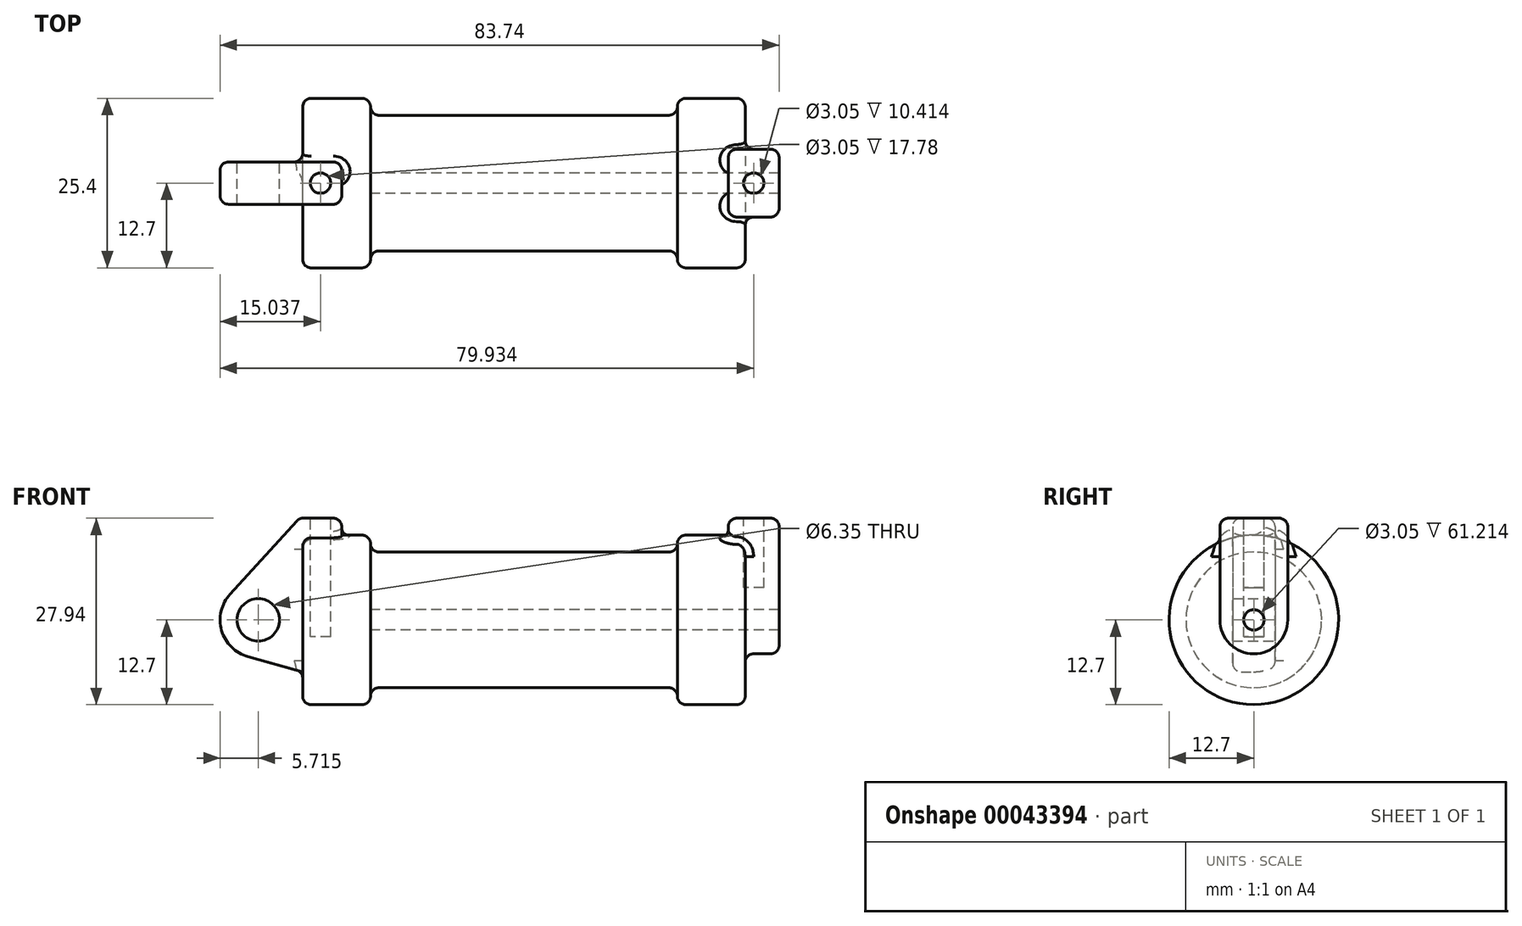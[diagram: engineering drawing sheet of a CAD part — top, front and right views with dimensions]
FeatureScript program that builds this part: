
annotation { "Feature Type Name" : "Feature", "Feature Type Description" : "" }
export const myFeature = defineFeature(function(context is Context, id is Id, definition is map)
    precondition{}
    {
        {
            var Q0;
            Q0=qCreatedBy(makeId("Front.planeOp"),FACE);
            var sketch = newSketch(context, id + "F0", { "sketchPlane" : qUnion([Q0])});
            skLineSegment(sketch, "E0", {"start": v(0, 0) * mm, "end": v(0, 12.7) * mm});
            skLineSegment(sketch, "E1", {"start": v(0, 12.7) * mm, "end": v(10.16, 12.7) * mm});
            skLineSegment(sketch, "E2", {"start": v(10.16, 12.7) * mm, "end": v(10.16, 10.16) * mm});
            skLineSegment(sketch, "E3", {"start": v(10.16, 10.16) * mm, "end": v(56.13, 10.16) * mm});
            skLineSegment(sketch, "E4", {"start": v(56.13, 10.16) * mm, "end": v(56.13, 12.7) * mm});
            skLineSegment(sketch, "E5", {"start": v(56.13, 12.7) * mm, "end": v(66.3, 12.7) * mm});
            skLineSegment(sketch, "E6", {"start": v(66.3, 12.7) * mm, "end": v(66.3, 0) * mm});
            skLineSegment(sketch, "E7", {"start": v(66.3, 0) * mm, "end": v(0, 0) * mm});
            skLineSegment(sketch, "E8", {"start": v(5.84, 15.24) * mm, "end": v(-0.5, 15.24) * mm});
            skLineSegment(sketch, "E9", {"start": v(-0.5, 15.24) * mm, "end": v(-10.88, 3.85) * mm});
            skLineSegment(sketch, "E10", {"start": v(0, 0) * mm, "end": v(-6.65, 0) * mm});
            skCircle(sketch, "E11", {"center": v(-6.65, 0) * mm, "radius": 5.72 * mm});
            skCircle(sketch, "E12", {"center": v(-6.65, 0) * mm, "radius": 3.18 * mm});
            skLineSegment(sketch, "E13", {"start": v(5.84, 15.24) * mm, "end": v(5.84, -9.4) * mm});
            skLineSegment(sketch, "E14", {"start": v(5.84, -9.4) * mm, "end": v(-8.18, -5.5) * mm});
            skSolve(sketch);
        }
        {
            var Q0;
            {var subQ6=sQuery(id+"F0.wireOp",EDGE,"E2");Q0=makeQuery(id+"F0.imprint","IMPRINT",FACE,{"disambiguationData":[TD([[makeQuery(id+"F0.imprint","IMPRINT",EDGE,{"derivedFrom":subQ6}),-1.0]])]});}
            var Q1;
            {var subQ5=sQuery(id+"F0.wireOp",EDGE,"E0");Q1=makeQuery(id+"F0.imprint","IMPRINT",FACE,{"disambiguationData":[TD([[makeQuery(id+"F0.imprint","IMPRINT",EDGE,{"derivedFrom":subQ5}),-1.0]])]});}
            var Q2;
            Q2=sQuery(id+"F0.wireOp",EDGE,"E7");
            revolve(context, id + "F1", {"entities" : qUnion([Q0, Q1]), "axis" : qUnion([Q2]), "revolveType" : RevolveType.FULL});
        }
        {
            var Q0;
            {var subQ8=sQuery(id+"F0.wireOp",EDGE,"E0");Q0=makeQuery(id+"F0.imprint","IMPRINT",FACE,{"disambiguationData":[TD([[makeQuery(id+"F0.imprint","IMPRINT",EDGE,{"derivedFrom":subQ8}),1.0]])]});}
            var Q1;
            {var subQ0=sQuery(id+"F0.wireOp",EDGE,"E12");Q1=makeQuery(id+"F0.imprint","IMPRINT",FACE,{"disambiguationData":[TD([[makeQuery(id+"F0.imprint","IMPRINT",EDGE,{"derivedFrom":subQ0}),-1.0]])]});}
            var Q2;
            {var subQ0=sQuery(id+"F0.wireOp",EDGE,"E14");Q2=makeQuery(id+"F0.imprint","IMPRINT",FACE,{"disambiguationData":[TD([[makeQuery(id+"F0.imprint","IMPRINT",EDGE,{"derivedFrom":subQ0}),-1.0]])]});}
            var Q3;
            {var subQ5=sQuery(id+"F0.wireOp",EDGE,"E0");Q3=makeQuery(id+"F0.imprint","IMPRINT",FACE,{"disambiguationData":[TD([[makeQuery(id+"F0.imprint","IMPRINT",EDGE,{"derivedFrom":subQ5}),-1.0]])]});}
            extrude(context, id + "F2", {"entities" : qUnion([Q0, Q1, Q2, Q3]), "operationType" : NewBodyOperationType.ADD, "endBound" : BoundingType.SYMMETRIC, "depth" : 6.35 * mm});
        }
        {
            var Q0;
            Q0=makeQuery(id+"F1.opRevolve","SWEPT_FACE",FACE,{"disambiguationData":[OSD([sQuery(id+"F0.wireOp",EDGE,"E6")])]});
            var sketch = newSketch(context, id + "F3", { "sketchPlane" : qUnion([Q0])});
            skCircle(sketch, "E15", {"center": v(0, 0) * mm, "radius": 5.08 * mm});
            skCircle(sketch, "E16", {"center": v(0, 0) * mm, "radius": 1.52 * mm});
            skLineSegment(sketch, "E17", {"start": v(-5.08, 0) * mm, "end": v(-5.08, 15.24) * mm});
            skLineSegment(sketch, "E18", {"start": v(-5.08, 15.24) * mm, "end": v(5.08, 15.24) * mm});
            skLineSegment(sketch, "E19", {"start": v(5.08, 15.24) * mm, "end": v(5.08, 0) * mm});
            skSolve(sketch);
        }
        {
            var Q0;
            Q0=makeQuery(id+"F3.imprint","IMPRINT",FACE,{"disambiguationData":[TD([[makeQuery(id+"F3.imprint","IMPRINT",EDGE,{"derivedFrom":sQuery(id+"F3.wireOp",EDGE,"E16")}),-1.0]])]});
            var Q1;
            {var subQ3=sQuery(id+"F3.wireOp",EDGE,"E17");var subQ5=sQuery(id+"F3.wireOp",EDGE,"E15");var subQ7=makeQuery(id+"F3.imprint","INTERSECT",VERTEX,{"derivedFrom":[subQ5,subQ3]});Q1=makeQuery(id+"F3.imprint","IMPRINT",FACE,{"disambiguationData":[TD([[makeQuery(id+"F3.imprint","IMPRINT",EDGE,{"disambiguationData":[TD([[subQ7,1.0]])],"derivedFrom":subQ5}),-1.0]])]});}
            var Q2;
            {var subQ5=sQuery(id+"F3.wireOp",EDGE,"E18");Q2=makeQuery(id+"F3.imprint","IMPRINT",FACE,{"disambiguationData":[TD([[makeQuery(id+"F3.imprint","IMPRINT",EDGE,{"derivedFrom":subQ5}),-1.0]])]});}
            extrude(context, id + "F4", {"entities" : qUnion([Q0, Q1, Q2]), "operationType" : NewBodyOperationType.ADD, "depth" : 5.08 * mm});
        }
        {
            var Q0;
            {var subQ0=sQuery(id+"F3.wireOp",EDGE,"E15");var subQ3=sQuery(id+"F3.wireOp",EDGE,"E17");var subQ4=makeQuery(id+"F3.imprint","INTERSECT",VERTEX,{"derivedFrom":[subQ0,subQ3]});var subQ5=makeQuery(id+"F3.imprint","IMPRINT",EDGE,{"disambiguationData":[TD([[subQ4,1.0]])],"derivedFrom":subQ0});var subQ10=sQuery(id+"F3.wireOp",EDGE,"E18");Q0=qUnion([makeQuery(id+"F3.imprint","IMPRINT",FACE,{"disambiguationData":[TD([[makeQuery(id+"F3.imprint","IMPRINT",EDGE,{"derivedFrom":sQuery(id+"F3.wireOp",EDGE,"E16")}),-1.0]])]}),makeQuery(id+"F3.imprint","IMPRINT",FACE,{"disambiguationData":[TD([[makeQuery(id+"F3.imprint","IMPRINT",EDGE,{"derivedFrom":subQ10}),-1.0]])]}),makeQuery(id+"F3.imprint","IMPRINT",FACE,{"disambiguationData":[TD([[subQ5,-1.0]])]})]);}
            extrude(context, id + "F5", {"entities" : qUnion([Q0]), "operationType" : NewBodyOperationType.ADD, "oppositeDirection" : true, "depth" : 2.54 * mm});
        }
        {
            var Q0;
            Q0=makeQuery(id+"F4.boolean.opBoolean","SPLIT",FACE,{"disambiguationData":[TD([makeQuery(id+"F4.opExtrude","SWEPT_FACE",FACE,{"disambiguationData":[OSD([sQuery(id+"F3.wireOp",EDGE,"E16")])]})])],"derivedFrom":makeQuery(id+"F1.opRevolve","SWEPT_FACE",FACE,{"disambiguationData":[OSD([sQuery(id+"F0.wireOp",EDGE,"E6")])]})});
            var Q1;
            Q1=makeQuery(id+"F1.opRevolve","SWEPT_FACE",FACE,{"disambiguationData":[OSD([sQuery(id+"F0.wireOp",EDGE,"E2")])]});
            extrude(context, id + "F6", {"entities" : qUnion([Q0]), "operationType" : NewBodyOperationType.REMOVE, "endBound" : BoundingType.UP_TO_SURFACE, "oppositeDirection" : true, "endBoundEntityFace" : qUnion([Q1]), "depth" : 25.4 * mm});
        }
        {
            var Q0;
            {var subQ0=sQuery(id+"F3.wireOp",EDGE,"E18");Q0=makeQuery(id+"F5.boolean.opBoolean","MERGE",FACE,{"derivedFrom":[makeQuery(id+"F4.opExtrude","SWEPT_FACE",FACE,{"disambiguationData":[OSD([subQ0])]}),makeQuery(id+"F5.opExtrude","SWEPT_FACE",FACE,{"disambiguationData":[OSD([subQ0])]})]});}
            var sketch = newSketch(context, id + "F7", { "sketchPlane" : qUnion([Q0])});
            skLineSegment(sketch, "E20", {"start": v(63.75, -5.08) * mm, "end": v(71.37, 5.08) * mm, "construction": true});
            skCircle(sketch, "E21", {"center": v(67.56, 0) * mm, "radius": 1.52 * mm});
            skSolve(sketch);
        }
        {
            var Q0;
            Q0=qSketchRegion(id+"F7",true);
            extrude(context, id + "F8", {"entities" : qUnion([Q0]), "operationType" : NewBodyOperationType.REMOVE, "oppositeDirection" : true, "depth" : 10.4 * mm});
        }
        {
            var Q0;
            Q0=makeQuery(id+"F2.opExtrude","SWEPT_FACE",FACE,{"disambiguationData":[OSD([sQuery(id+"F0.wireOp",EDGE,"E8")])]});
            var sketch = newSketch(context, id + "F9", { "sketchPlane" : qUnion([Q0])});
            skLineSegment(sketch, "E22", {"start": v(-0.5, -3.18) * mm, "end": v(5.84, 3.18) * mm, "construction": true});
            skCircle(sketch, "E23", {"center": v(2.67, 0) * mm, "radius": 1.52 * mm});
            skSolve(sketch);
        }
        {
            var Q0;
            Q0=makeQuery(id+"F9.imprint","IMPRINT",FACE,{"disambiguationData":[TD([[makeQuery(id+"F9.imprint","IMPRINT",EDGE,{"derivedFrom":sQuery(id+"F9.wireOp",EDGE,"E23")}),1.0]])]});
            extrude(context, id + "F10", {"entities" : qUnion([Q0]), "operationType" : NewBodyOperationType.REMOVE, "oppositeDirection" : true, "depth" : 17.78 * mm});
        }
        {
            var Q0;
            Q0=makeQuery(id+"F2.opExtrude","SWEPT_EDGE",EDGE,{"disambiguationData":[OSD([sQuery(id+"F0.wireOp",EDGE,"E8"),sQuery(id+"F0.wireOp",EDGE,"E9")])]});
            var Q1;
            Q1=makeQuery(id+"F2.opExtrude","SWEPT_EDGE",EDGE,{"disambiguationData":[OSD([sQuery(id+"F0.wireOp",EDGE,"E8"),sQuery(id+"F0.wireOp",EDGE,"E13")])]});
            var Q2;
            Q2=makeQuery(id+"F2.opExtrude","CAP_EDGE",EDGE,{"disambiguationData":[OSD([sQuery(id+"F0.wireOp",EDGE,"E9")])],"isStart":false});
            var Q3;
            Q3=makeQuery(id+"F1.opRevolve","SWEPT_EDGE",EDGE,{"disambiguationData":[OSD([sQuery(id+"F0.wireOp",EDGE,"E0"),sQuery(id+"F0.wireOp",EDGE,"E1")])]});
            var Q4;
            Q4=makeQuery(id+"F1.opRevolve","SWEPT_EDGE",EDGE,{"disambiguationData":[OSD([sQuery(id+"F0.wireOp",EDGE,"E1"),sQuery(id+"F0.wireOp",EDGE,"E2")])]});
            var Q5;
            Q5=makeQuery(id+"F2.opExtrude","CAP_EDGE",EDGE,{"disambiguationData":[OSD([sQuery(id+"F0.wireOp",EDGE,"E13")])],"isStart":false});
            var Q6;
            Q6=makeQuery(id+"F2.opExtrude","CAP_EDGE",EDGE,{"disambiguationData":[OSD([sQuery(id+"F0.wireOp",EDGE,"E9")])],"isStart":true});
            var Q7;
            Q7=makeQuery(id+"F2.boolean.opBoolean","INTERSECT",EDGE,{"derivedFrom":[makeQuery(id+"F1.opRevolve","SWEPT_FACE",FACE,{"disambiguationData":[OSD([sQuery(id+"F0.wireOp",EDGE,"E1")])]}),makeQuery(id+"F2.opExtrude","CAP_FACE",FACE,{"disambiguationData":[OSD([sQuery(id+"F0.wireOp",EDGE,"E8"),sQuery(id+"F0.wireOp",EDGE,"E9"),sQuery(id+"F0.wireOp",EDGE,"E11"),sQuery(id+"F0.wireOp",EDGE,"E12"),sQuery(id+"F0.wireOp",EDGE,"E13"),sQuery(id+"F0.wireOp",EDGE,"E14")])],"isStart":true})]});
            var Q8;
            Q8=makeQuery(id+"F2.boolean.opBoolean","INTERSECT",EDGE,{"derivedFrom":[makeQuery(id+"F1.opRevolve","SWEPT_FACE",FACE,{"disambiguationData":[OSD([sQuery(id+"F0.wireOp",EDGE,"E0")])]}),makeQuery(id+"F2.opExtrude","CAP_FACE",FACE,{"disambiguationData":[OSD([sQuery(id+"F0.wireOp",EDGE,"E8"),sQuery(id+"F0.wireOp",EDGE,"E9"),sQuery(id+"F0.wireOp",EDGE,"E11"),sQuery(id+"F0.wireOp",EDGE,"E12"),sQuery(id+"F0.wireOp",EDGE,"E13"),sQuery(id+"F0.wireOp",EDGE,"E14")])],"isStart":true})]});
            var Q9;
            Q9=makeQuery(id+"F2.opExtrude","CAP_EDGE",EDGE,{"disambiguationData":[OSD([sQuery(id+"F0.wireOp",EDGE,"E8")])],"isStart":true});
            var Q10;
            Q10=makeQuery(id+"F2.opExtrude","CAP_EDGE",EDGE,{"disambiguationData":[OSD([sQuery(id+"F0.wireOp",EDGE,"E13")])],"isStart":true});
            var Q11;
            Q11=makeQuery(id+"F2.opExtrude","CAP_EDGE",EDGE,{"disambiguationData":[OSD([sQuery(id+"F0.wireOp",EDGE,"E8")])],"isStart":false});
            fillet(context, id + "F11", {"entities" : qUnion([Q0, Q1, Q2, Q3, Q4, Q5, Q6, Q7, Q8, Q9, Q10, Q11]), "radius" : 1.27 * mm, "tangentPropagation" : true, "allowEdgeOverflow" : false});
        }
        {
            var Q0;
            Q0=makeQuery(id+"F1.opRevolve","SWEPT_EDGE",EDGE,{"disambiguationData":[OSD([sQuery(id+"F0.wireOp",EDGE,"E2"),sQuery(id+"F0.wireOp",EDGE,"E3")])]});
            var Q1;
            Q1=makeQuery(id+"F1.opRevolve","SWEPT_EDGE",EDGE,{"disambiguationData":[OSD([sQuery(id+"F0.wireOp",EDGE,"E3"),sQuery(id+"F0.wireOp",EDGE,"E4")])]});
            fillet(context, id + "F12", {"entities" : qUnion([Q0, Q1]), "radius" : 1.27 * mm, "tangentPropagation" : true, "allowEdgeOverflow" : false});
        }
        {
            var Q0;
            {var subQ0=sQuery(id+"F3.wireOp",EDGE,"E17");Q0=makeQuery(id+"F5.boolean.opBoolean","MERGE",FACE,{"derivedFrom":[makeQuery(id+"F4.opExtrude","SWEPT_FACE",FACE,{"disambiguationData":[OSD([subQ0])]}),makeQuery(id+"F5.opExtrude","SWEPT_FACE",FACE,{"disambiguationData":[OSD([subQ0])]})]});}
            var Q1;
            {var subQ0=sQuery(id+"F3.wireOp",EDGE,"E19");Q1=makeQuery(id+"F5.boolean.opBoolean","MERGE",FACE,{"derivedFrom":[makeQuery(id+"F4.opExtrude","SWEPT_FACE",FACE,{"disambiguationData":[OSD([subQ0])]}),makeQuery(id+"F5.opExtrude","SWEPT_FACE",FACE,{"disambiguationData":[OSD([subQ0])]})]});}
            var Q2;
            Q2=makeQuery(id+"F4.opExtrude","CAP_EDGE",EDGE,{"disambiguationData":[OSD([sQuery(id+"F3.wireOp",EDGE,"E18")])],"isStart":false});
            var Q3;
            Q3=makeQuery(id+"F5.opExtrude","CAP_EDGE",EDGE,{"disambiguationData":[OSD([sQuery(id+"F3.wireOp",EDGE,"E18")])],"isStart":false});
            var Q4;
            Q4=makeQuery(id+"F4.boolean.opBoolean","SPLIT",FACE,{"disambiguationData":[TD([makeQuery(id+"F1.opRevolve","SWEPT_FACE",FACE,{"disambiguationData":[OSD([sQuery(id+"F0.wireOp",EDGE,"E5")])]})])],"derivedFrom":makeQuery(id+"F1.opRevolve","SWEPT_FACE",FACE,{"disambiguationData":[OSD([sQuery(id+"F0.wireOp",EDGE,"E6")])]})});
            var Q5;
            Q5=makeQuery(id+"F1.opRevolve","SWEPT_EDGE",EDGE,{"disambiguationData":[OSD([sQuery(id+"F0.wireOp",EDGE,"E4"),sQuery(id+"F0.wireOp",EDGE,"E5")])]});
            fillet(context, id + "F13", {"entities" : qUnion([Q0, Q1, Q2, Q3, Q4, Q5]), "radius" : 1.27 * mm, "tangentPropagation" : true, "allowEdgeOverflow" : false});
        }
    });
